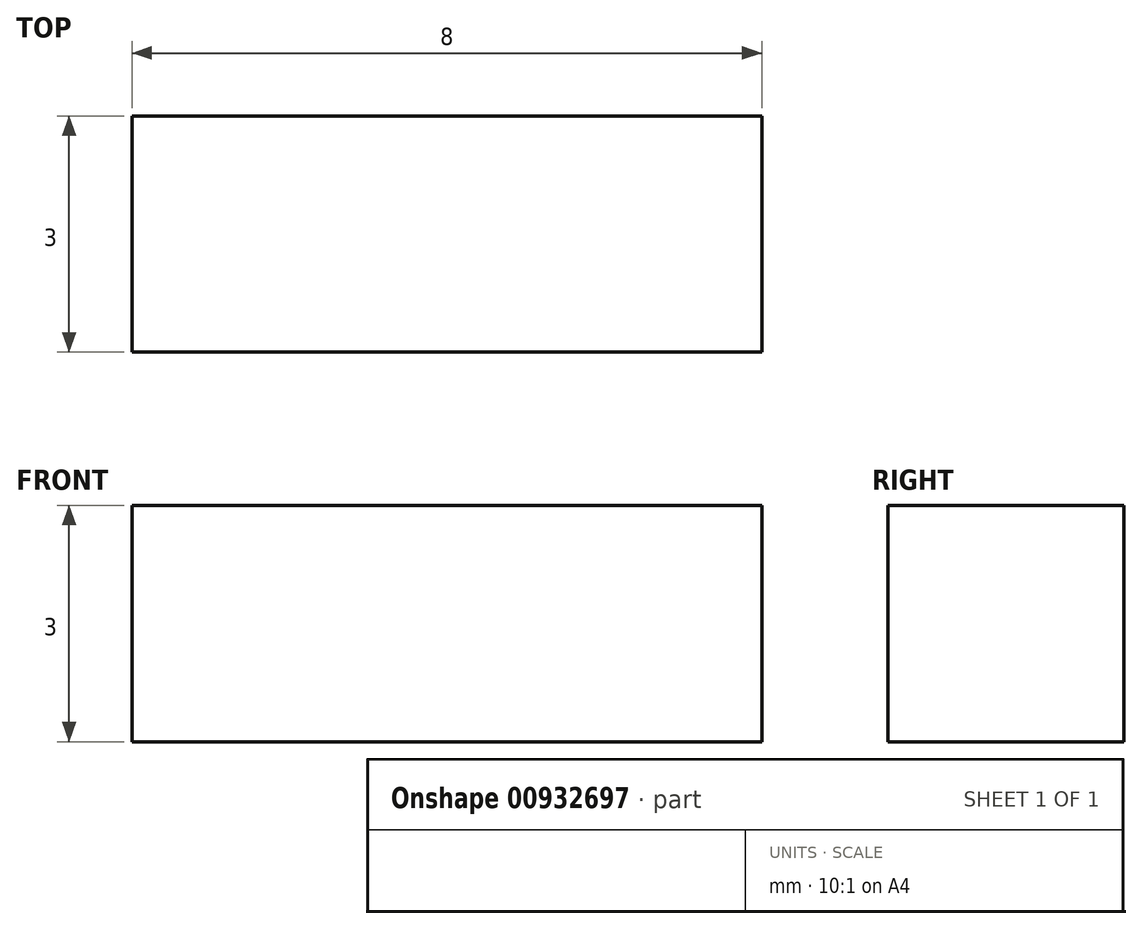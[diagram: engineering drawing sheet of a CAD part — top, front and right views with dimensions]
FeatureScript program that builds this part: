
annotation { "Feature Type Name" : "Feature", "Feature Type Description" : "" }
export const myFeature = defineFeature(function(context is Context, id is Id, definition is map)
    precondition{}
    {
        {
            var Q0;
            Q0=qCreatedBy(makeId("Top.planeOp"),FACE);
            var sketch = newSketch(context, id + "F0", { "sketchPlane" : qUnion([Q0])});
            skLineSegment(sketch, "E0.bottom", {"start": v(-4, 1.5) * mm, "end": v(4, 1.5) * mm});
            skLineSegment(sketch, "E0.top", {"start": v(-4, -1.5) * mm, "end": v(4, -1.5) * mm});
            skLineSegment(sketch, "E0.left", {"start": v(-4, 1.5) * mm, "end": v(-4, -1.5) * mm});
            skLineSegment(sketch, "E0.right", {"start": v(4, 1.5) * mm, "end": v(4, -1.5) * mm});
            skSolve(sketch);
        }
        {
            var Q0;
            Q0=qSketchRegion(id+"F0",true);
            extrude(context, id + "F1", {"entities" : qUnion([Q0]), "depth" : 3 * mm, "offsetDistance" : 25 * mm});
        }
    });
